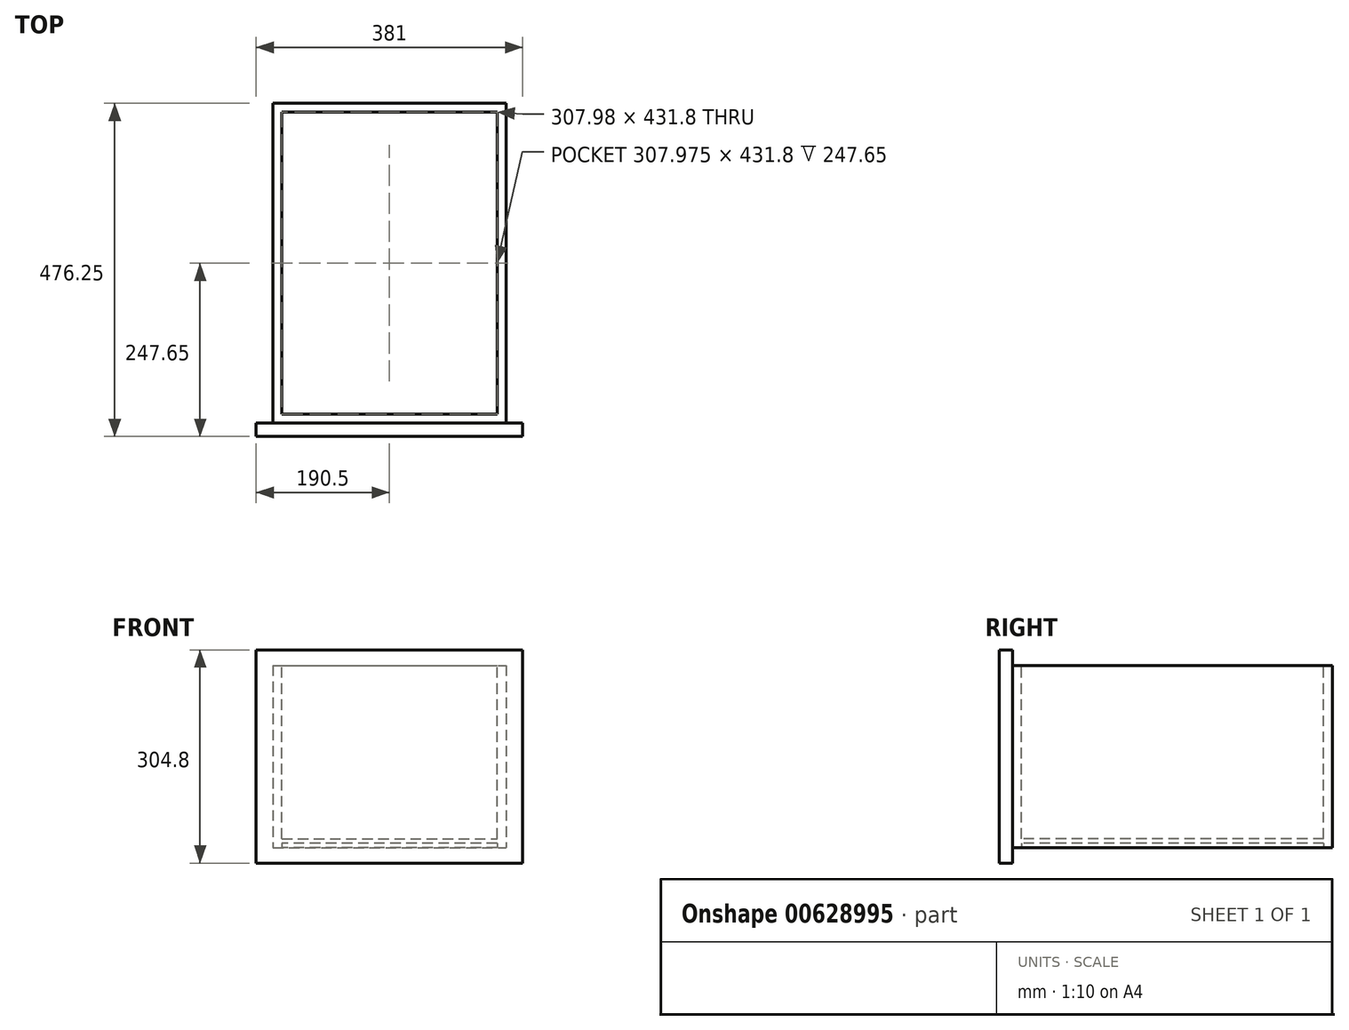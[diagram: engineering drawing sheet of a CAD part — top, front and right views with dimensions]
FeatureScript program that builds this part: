
annotation { "Feature Type Name" : "Feature", "Feature Type Description" : "" }
export const myFeature = defineFeature(function(context is Context, id is Id, definition is map)
    precondition{}
    {
        {
            var Q0;
            Q0=qCreatedBy(makeId("Front.planeOp"),FACE);
            var sketch = newSketch(context, id + "F0", { "sketchPlane" : qUnion([Q0])});
            skLineSegment(sketch, "E0.bottom", {"start": v(-190.5, 152.4) * mm, "end": v(190.5, 152.4) * mm});
            skLineSegment(sketch, "E0.top", {"start": v(-190.5, -152.4) * mm, "end": v(190.5, -152.4) * mm});
            skLineSegment(sketch, "E0.left", {"start": v(-190.5, 152.4) * mm, "end": v(-190.5, -152.4) * mm});
            skLineSegment(sketch, "E0.right", {"start": v(190.5, 152.4) * mm, "end": v(190.5, -152.4) * mm});
            skPoint(sketch, "E0.middle", {"position": v(0, 0) * mm});
            skSolve(sketch);
        }
        {
            var Q0;
            Q0=makeQuery(id+"F0.imprint","IMPRINT",FACE,{"disambiguationData":[TD([[makeQuery(id+"F0.imprint","IMPRINT",EDGE,{"derivedFrom":sQuery(id+"F0.wireOp",EDGE,"E0.bottom")}),-1.0]])]});
            extrude(context, id + "F1", {"entities" : qUnion([Q0]), "depth" : 19.05 * mm, "offsetDistance" : 25.4 * mm});
        }
        {
            var Q0;
            Q0=makeQuery(id+"F1.opExtrude","CAP_FACE",FACE,{"disambiguationData":[OSD([sQuery(id+"F0.wireOp",EDGE,"E0.bottom"),sQuery(id+"F0.wireOp",EDGE,"E0.top"),sQuery(id+"F0.wireOp",EDGE,"E0.left"),sQuery(id+"F0.wireOp",EDGE,"E0.right")])],"isStart":true});
            var sketch = newSketch(context, id + "F2", { "sketchPlane" : qUnion([Q0])});
            skLineSegment(sketch, "E1", {"start": v(0, -152.4) * mm, "end": v(0, 0) * mm});
            skLineSegment(sketch, "E2.bottom", {"start": v(166.69, 130.18) * mm, "end": v(-166.69, 130.18) * mm});
            skLineSegment(sketch, "E2.top", {"start": v(166.69, -130.18) * mm, "end": v(-166.69, -130.17) * mm});
            skLineSegment(sketch, "E2.left", {"start": v(166.69, 130.18) * mm, "end": v(166.69, -130.17) * mm});
            skLineSegment(sketch, "E2.right", {"start": v(-166.69, 130.18) * mm, "end": v(-166.69, -130.17) * mm});
            skPoint(sketch, "E2.middle", {"position": v(0, 0) * mm});
            skSolve(sketch);
        }
        {
            var Q0;
            Q0=makeQuery(id+"F2.imprint","IMPRINT",FACE,{"disambiguationData":[TD([[makeQuery(id+"F2.imprint","IMPRINT",EDGE,{"derivedFrom":sQuery(id+"F2.wireOp",EDGE,"E2.bottom")}),1.0]])]});
            extrude(context, id + "F3", {"entities" : qUnion([Q0]), "operationType" : NewBodyOperationType.ADD, "depth" : 457.2 * mm, "offsetDistance" : 25.4 * mm});
        }
        {
            var Q0;
            Q0=makeQuery(id+"F3.opExtrude","SWEPT_FACE",FACE,{"disambiguationData":[OSD([sQuery(id+"F2.wireOp",EDGE,"E2.top")])]});
            var sketch = newSketch(context, id + "F4", { "sketchPlane" : qUnion([Q0])});
            skLineSegment(sketch, "E3.bottom", {"start": v(153.99, -444.5) * mm, "end": v(-153.99, -444.5) * mm});
            skLineSegment(sketch, "E3.top", {"start": v(153.99, -12.7) * mm, "end": v(-153.99, -12.7) * mm});
            skLineSegment(sketch, "E3.left", {"start": v(153.99, -444.5) * mm, "end": v(153.99, -12.7) * mm});
            skLineSegment(sketch, "E3.right", {"start": v(-153.99, -444.5) * mm, "end": v(-153.99, -12.7) * mm});
            skPoint(sketch, "E3.middle", {"position": v(0, -228.6) * mm});
            skPoint(sketch, "E3.middle.positionSnap0", {"position": v(166.69, -228.6) * mm});
            skPoint(sketch, "E3.centerSnap0", {"position": v(166.69, -228.6) * mm});
            skSolve(sketch);
        }
        {
            var Q0;
            Q0=makeQuery(id+"F4.imprint","IMPRINT",FACE,{"disambiguationData":[TD([[makeQuery(id+"F4.imprint","IMPRINT",EDGE,{"derivedFrom":sQuery(id+"F4.wireOp",EDGE,"E3.bottom")}),-1.0]])]});
            extrude(context, id + "F5", {"entities" : qUnion([Q0]), "operationType" : NewBodyOperationType.REMOVE, "oppositeDirection" : true, "depth" : 6.35 * mm, "offsetDistance" : 25.4 * mm});
        }
        {
            var Q0;
            Q0=makeQuery(id+"F3.opExtrude","SWEPT_FACE",FACE,{"disambiguationData":[OSD([sQuery(id+"F2.wireOp",EDGE,"E2.bottom")])]});
            var sketch = newSketch(context, id + "F6", { "sketchPlane" : qUnion([Q0])});
            skLineSegment(sketch, "E4.bottom", {"start": v(-153.99, 444.5) * mm, "end": v(153.99, 444.5) * mm});
            skLineSegment(sketch, "E4.top", {"start": v(-153.99, 12.7) * mm, "end": v(153.99, 12.7) * mm});
            skLineSegment(sketch, "E4.left", {"start": v(-153.99, 444.5) * mm, "end": v(-153.99, 12.7) * mm});
            skLineSegment(sketch, "E4.right", {"start": v(153.99, 444.5) * mm, "end": v(153.99, 12.7) * mm});
            skPoint(sketch, "E4.middle", {"position": v(0, 228.6) * mm});
            skPoint(sketch, "E4.middle.positionSnap0", {"position": v(-166.69, 228.6) * mm});
            skPoint(sketch, "E4.centerSnap0", {"position": v(-166.69, 228.6) * mm});
            skSolve(sketch);
        }
        {
            var Q0;
            Q0=makeQuery(id+"F6.imprint","IMPRINT",FACE,{"disambiguationData":[TD([[makeQuery(id+"F6.imprint","IMPRINT",EDGE,{"derivedFrom":sQuery(id+"F6.wireOp",EDGE,"E4.bottom")}),-1.0]])]});
            extrude(context, id + "F7", {"entities" : qUnion([Q0]), "operationType" : NewBodyOperationType.REMOVE, "oppositeDirection" : true, "depth" : 247.65 * mm, "offsetDistance" : 25.4 * mm});
        }
    });
